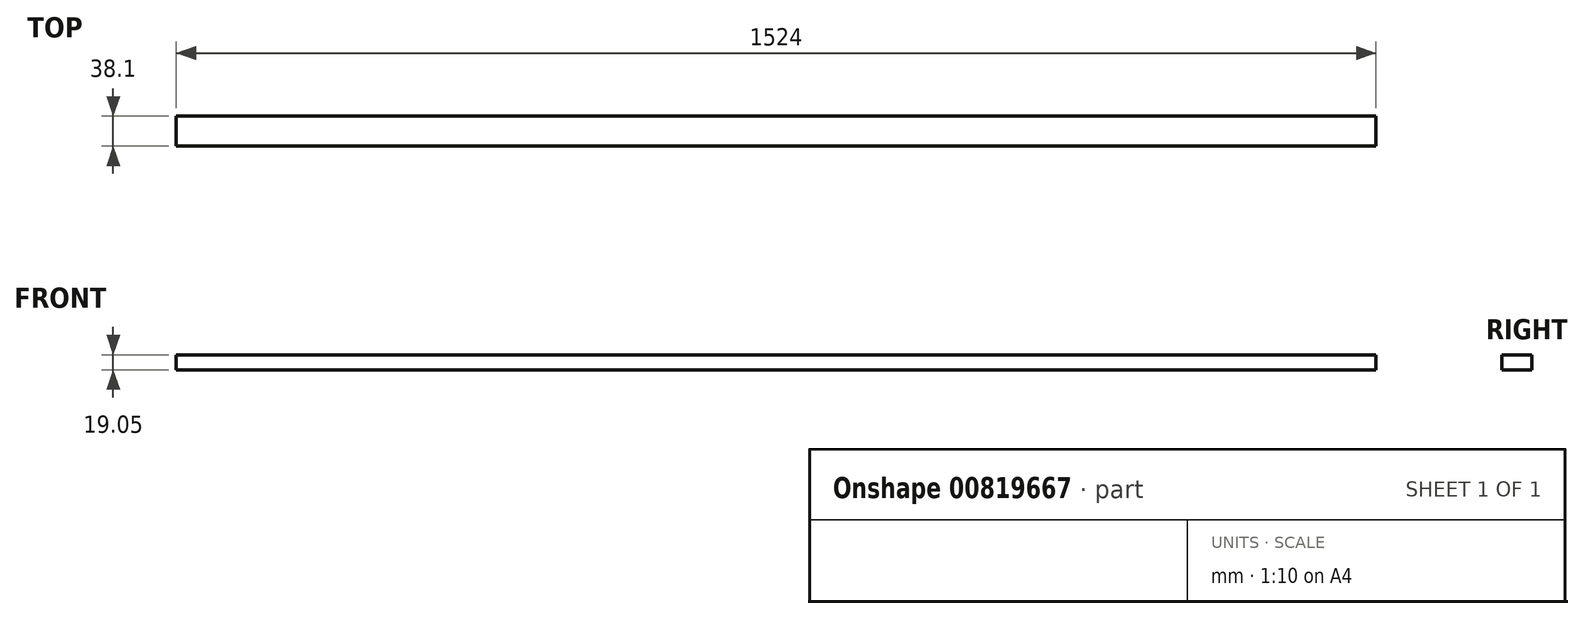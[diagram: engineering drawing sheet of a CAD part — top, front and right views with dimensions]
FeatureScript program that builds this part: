
annotation { "Feature Type Name" : "Feature", "Feature Type Description" : "" }
export const myFeature = defineFeature(function(context is Context, id is Id, definition is map)
    precondition{}
    {
        {
            var Q0;
            Q0=qCreatedBy(makeId("Front.planeOp"),FACE);
            var sketch = newSketch(context, id + "F0", { "sketchPlane" : qUnion([Q0])});
            skLineSegment(sketch, "E0.bottom", {"start": v(1456.34, 0) * mm, "end": v(-67.66, 0) * mm});
            skLineSegment(sketch, "E0.top", {"start": v(1456.34, 19.05) * mm, "end": v(-67.66, 19.05) * mm});
            skLineSegment(sketch, "E0.left", {"start": v(1456.34, 0) * mm, "end": v(1456.34, 19.05) * mm});
            skLineSegment(sketch, "E0.right", {"start": v(-67.66, 0) * mm, "end": v(-67.66, 19.05) * mm});
            skSolve(sketch);
        }
        {
            var Q0;
            Q0 = qSketchRegion(id + "F0", true);
            extrude(context, id + "F1", {"entities" : qUnion([Q0]), "depth" : 38.1 * mm, "offsetDistance" : 25.4 * mm});
        }
    });
